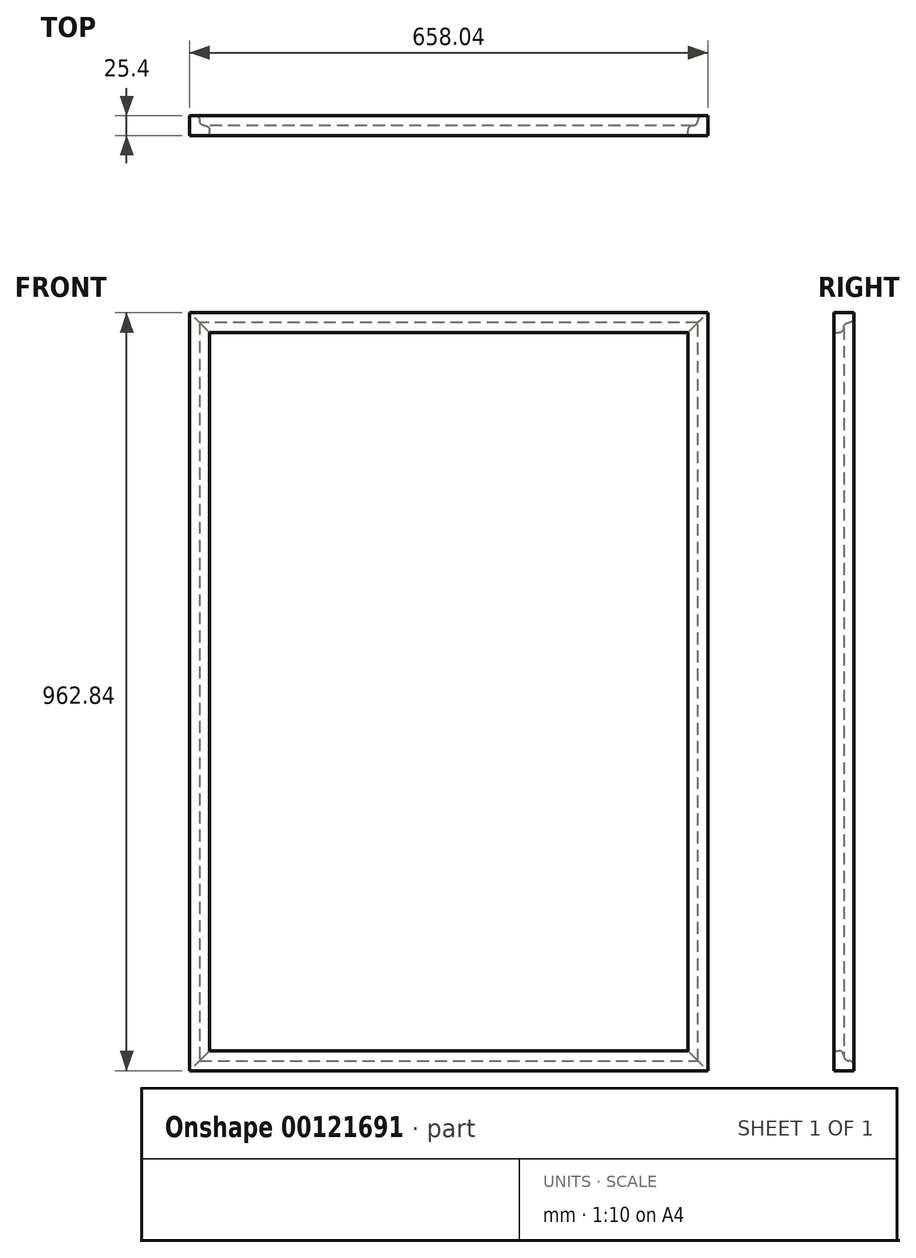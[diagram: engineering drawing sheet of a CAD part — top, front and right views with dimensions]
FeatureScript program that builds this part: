
annotation { "Feature Type Name" : "Feature", "Feature Type Description" : "" }
export const myFeature = defineFeature(function(context is Context, id is Id, definition is map)
    precondition{}
    {
        {
            var Q0;
            Q0=qCreatedBy(makeId("Front.planeOp"),FACE);
            var sketch = newSketch(context, id + "F0", { "sketchPlane" : qUnion([Q0])});
            skLineSegment(sketch, "E0.bottom", {"start": v(-345.62, 299.27) * mm, "end": v(263.98, 299.27) * mm});
            skLineSegment(sketch, "E0.top", {"start": v(-345.62, -615.13) * mm, "end": v(263.98, -615.13) * mm});
            skLineSegment(sketch, "E0.left", {"start": v(-345.62, 299.27) * mm, "end": v(-345.62, -615.13) * mm});
            skLineSegment(sketch, "E0.right", {"start": v(263.98, 299.27) * mm, "end": v(263.98, -615.13) * mm});
            skSolve(sketch);
        }
        {
            var Q0;
            Q0=qCreatedBy(makeId("Top.planeOp"),FACE);
            var sketch = newSketch(context, id + "F1", { "sketchPlane" : qUnion([Q0])});
            skLineSegment(sketch, "E1", {"start": v(288.2, 12.7) * mm, "end": v(288.2, -12.7) * mm});
            skLineSegment(sketch, "E2", {"start": v(288.2, -12.7) * mm, "end": v(262.8, -12.7) * mm});
            skLineSegment(sketch, "E3", {"start": v(262.8, -6.35) * mm, "end": v(262.8, -12.7) * mm});
            skLineSegment(sketch, "E4", {"start": v(288.2, 12.7) * mm, "end": v(281.85, 12.7) * mm});
            skArc(sketch, "E5", {"start": v(281.85, 12.7) * mm, "mid": v(277.36, 10.84) * mm, "end": v(275.5, 6.35) * mm});
            skArc(sketch, "E6", {"start": v(275.5, 6.35) * mm, "mid": v(273.64, 1.86) * mm, "end": v(269.15, 0) * mm});
            skArc(sketch, "E7", {"start": v(269.15, 0) * mm, "mid": v(264.66, -1.86) * mm, "end": v(262.8, -6.35) * mm});
            skPoint(sketch, "E8", {"position": v(262.8, -9.52) * mm});
            skSolve(sketch);
        }
        {
            var Q0;
            Q0=makeQuery(id+"F1.imprint","IMPRINT",FACE,{"disambiguationData":[TD([[makeQuery(id+"F1.imprint","IMPRINT",EDGE,{"derivedFrom":sQuery(id+"F1.wireOp",EDGE,"E1")}),-1.0]])]});
            var Q1;
            Q1=sQuery(id+"F0.wireOp",EDGE,"E0.right");
            var Q2;
            Q2=sQuery(id+"F0.wireOp",EDGE,"E0.top");
            var Q3;
            Q3=sQuery(id+"F0.wireOp",EDGE,"E0.left");
            var Q4;
            Q4=sQuery(id+"F0.wireOp",EDGE,"E0.bottom");
            sweep(context, id + "F2", {"profiles" : qUnion([Q0]), "path" : qUnion([Q1, Q2, Q3, Q4])});
        }
    });
